# Revit family: Elkay_Drinking-Water_Bottle-Filling-Stations_EZ_Onwall_St1_Asiapac
name_source: partatom
category: Plumbing Fixtures
units: mm (PartAtom-declared; Revit-internal decimal feet)

## family parameters
Always vertical = Yes
Cut with Voids When Loaded = No
Part Type = Normal
Room Calculation Point = No
Round Connector Dimension = Use Diameter
Shared = Yes
Work Plane-Based = No

## types (24) — shared parameters
Installation Location = Indoor
Manufacturer = Elkay
Mounting Type = Wall Mount (On Wall)
Number of Stations = 1
Top Logo Plate = Yes
Version = 1.0.0.0

## per-type parameters (varying)
| type | Activation by | Approx. Shipping Weight | Base With Out Grill | Basin3 | Bottle Filling Station Logo With Out Elkay | Bubbler Style | Chilling Capacity | Dimensions (L x W x H) | EZWSSMJO_Base | EZWSSMJO_plate1 | EZWSSMJO_plate2 | Finish | Finish_1 | Flexiguard Bubbler | Full Load Amps | GreenSpec & Sensor Logo | GreenSpec Logo | Power | Push Button | Rated Watts | Special Features | Top Elkay EZH2@Blue | Vandal Resistant | Without Elkay Top Basin |
| EZWSSMJO | Electronic Bottle Filler Sensor | 32 lbs | No | No | No | No Bubbler | Non-refrigerated | 17 15/16 inch x 8 3/16 inch x 25 7/16 inch | Yes | No | Yes | Stainless Steel | 304 Stainless Steel | No | 1 | No | Yes | 220V/50-60Hz | No | 15 | Antimicrobial, Green Ticker™, Hands Free, Laminar Flow, Real Drain | No | No | No |
| LZS8WSS2K | Electronic Bottle Filler Sensor With Electronic Front And Side Bubbler Pushbar | 71 lbs | Yes | Yes | Yes | Flexi-Guard ® Safety Bubbler | 8.0 GPH | 18 3/8 inch x 19 inch x 39 1/16 inch | No | No | No | Stainless Steel | 304 Stainless Steel | Yes | 3 | Yes | No | 220V/50Hz | Yes | 370 | Hands Free, Visual Filter Monitor, Filtered, Green Ticker™, Laminar Flow, Antimicrobial, Real Drain | Yes | No | Yes |
| LZS8WSVRL2K | Electronic Bottle Filler Sensor With Electronic Front And Side Bubbler Pushbar | 72 lbs | Yes | Yes | Yes | Vandal Resistant | 8.0 GPH | 18 3/8 inch x 19 inch x 39 1/16 inch | No | No | No | Light Gray Granite | Light Gray Granite | No | 3 | Yes | No | 220V/50Hz | Yes | 370 | Hands Free, Visual Filter Monitor, Filtered, Green Ticker™, Laminar Flow, Antimicrobial, Real Drain | Yes | Yes | Yes |
| LZS8WSVRS2K | Electronic Bottle Filler Sensor With Electronic Front And Side Bubbler Pushbar | 72 lbs | Yes | Yes | Yes | Vandal Resistant | 8.0 GPH | 18 3/8 inch x 19 inch x 39 1/16 inch | No | No | No | Stainless Steel | 304 Stainless Steel | No | 3 | Yes | No | 220V/50Hz | Yes | 370 | Hands Free, Visual Filter Monitor, Filtered, Green Ticker™, Laminar Flow, Antimicrobial, Real Drain | Yes | Yes | Yes |
| LZS8WSVRS3K | Electronic Bottle Filler Sensor With Electronic Front And Side Bubbler Pushbar | 72 lbs | Yes | Yes | Yes | Vandal Resistant | 8.0 GPH | 18 3/8 inch x 19 inch x 39 1/16 inch | No | No | No | Stainless Steel | 304 Stainless Steel | No | 3 | Yes | No | 220V/60Hz | Yes | 370 | Hands Free, Visual Filter Monitor, Filtered, Green Ticker™, Laminar Flow, Antimicrobial, Real Drain | Yes | Yes | Yes |
| LZSDWSL2K | Electronic Bottle Filler Sensor With Electronic Front And Side Bubbler Pushbar | 45 lbs | Yes | Yes | Yes | Flexi-Guard ® Safety Bubbler | Non-refrigerated | 18 3/8 inch x 19 inch x 39 1/16 inch | No | No | No | Light Gray Granite | Light Gray Granite | Yes | 2 | Yes | No | 220V/50Hz | Yes | 15 | Hands Free, Visual Filter Monitor, Filtered, Green Ticker™, Laminar Flow, Antimicrobial, Real Drain | Yes | No | Yes |
| LZSDWSL3K | Electronic Bottle Filler Sensor With Electronic Front And Side Bubbler Pushbar | 45 lbs | Yes | Yes | Yes | Flexi-Guard ® Safety Bubbler | Non-refrigerated | 18 3/8 inch x 19 inch x 39 1/16 inch | No | No | No | Light Gray Granite | Light Gray Granite | Yes | 2 | Yes | No | 220V/60Hz | Yes | 15 | Hands Free, Visual Filter Monitor, Filtered, Green Ticker™, Laminar Flow, Antimicrobial, Real Drain | Yes | No | Yes |
| LZSDWSS2K | Electronic Bottle Filler Sensor With Electronic Front And Side Bubbler Pushbar | 45 lbs | Yes | Yes | Yes | Flexi-Guard ® Safety Bubbler | Non-refrigerated | 18 3/8 inch x 19 inch x 39 1/16 inch | No | No | No | Stainless Steel | 304 Stainless Steel | No | 2 | Yes | No | 220V/50Hz | Yes | 15 | Hands Free, Visual Filter Monitor, Filtered, Green Ticker™, Laminar Flow, Antimicrobial, Real Drain | Yes | Yes | Yes |
| LZSDWSS3K | Electronic Bottle Filler Sensor With Electronic Front And Side Bubbler Pushbar | 45 lbs | Yes | Yes | Yes | Flexi-Guard ® Safety Bubbler | Non-refrigerated | 18 3/8 inch x 19 inch x 39 1/16 inch | No | No | No | Stainless Steel | 304 Stainless Steel | No | 2 | Yes | No | 220V/60Hz | Yes | 15 | Hands Free, Visual Filter Monitor, Filtered, Green Ticker™, Laminar Flow, Antimicrobial, Real Drain | Yes | Yes | Yes |
| LZWSSMJO | Electronic Bottle Filler Sensor | 35 lbs | No | No | No | No Bubbler | Non-refrigerated | 17 15/16 inch x 83/16 inch x 25 7/16 inch | Yes | Yes | No | Stainless Steel | 304 Stainless Steel | No | 1 | No | Yes | 220V/50-60Hz | No | 15 | Hands Free, Visual Filter Monitor, Filtered, Green Ticker™, Laminar Flow, Antimicrobial, Real Drain | No | No | No |
| EZS8WSL2K | Electronic Bottle Filler Sensor with Electronic Front and Side Bubbler Pushbar | 68 lbs | Yes | Yes | Yes | Flexi-Guard ® Safety Bubbler | 8.0 GPH | 18 3/8 inch x 19 inch x 39 1/16 inch | No | No | No | Light Gray Granite | Light Gray Granite | Yes | 3 | No | Yes | 220V/50Hz | Yes | 370 | Antimicrobial, Green Ticker™, Hands Free, Laminar Flow, Real Drain | Yes | No | Yes |
| EZS8WSL3K | Electronic Bottle Filler Sensor with Electronic Front and Side Bubbler Pushbar | 68 lbs | Yes | Yes | Yes | Flexi-Guard ® Safety Bubbler | 8.0 GPH | 18 3/8 inch x 19 inch x 39 1/16 inch | No | No | No | Light Gray Granite | Light Gray Granite | Yes | 3 | No | Yes | 220V/60Hz | Yes | 370 | Antimicrobial, Green Ticker™, Hands Free, Laminar Flow, Real Drain | Yes | No | Yes |
| EZS8WSS2K | Electronic Bottle Filler Sensor with Electronic Front and Side Bubbler Pushbar | 68 lbs | Yes | Yes | Yes | Flexi-Guard ® Safety Bubbler | 8.0 GPH | 18 3/8 inch x 19 inch x 39 1/16 inch | No | No | No | Stainless Steel | 304 Stainless Steel | Yes | 3 | No | Yes | 220V/50Hz | Yes | 370 | Antimicrobial, Green Ticker™, Hands Free, Laminar Flow, Real Drain | Yes | No | Yes |
| EZS8WSS3K | Electronic Bottle Filler Sensor with Electronic Front and Side Bubbler Pushbar | 68 lbs | Yes | Yes | Yes | Flexi-Guard ® Safety Bubbler | 8.0 GPH | 18 3/8 inch x 19 inch x 39 1/16 inch | No | No | No | Stainless Steel | 304 Stainless Steel | Yes | 3 | No | Yes | 220V/60Hz | Yes | 370 | Antimicrobial, Green Ticker™, Hands Free, Laminar Flow, Real Drain | Yes | No | Yes |
| EZS8WSVRL2K | Electronic Bottle Filler Sensor with Electronic Front and Side Bubbler Pushbar | 69 lbs | Yes | Yes | Yes | Vandal Resistant | 8.0 GPH | 18 3/8 inch x 19 inch x 39 1/16 inch | No | No | No | Light Gray Granite | Light Gray Granite | No | 3 | No | Yes | 220V/50Hz | Yes | 370 | Antimicrobial, Green Ticker™, Hands Free, Laminar Flow, Real Drain | Yes | Yes | Yes |
| EZS8WSVRL3K | Electronic Bottle Filler Sensor with Electronic Front and Side Bubbler Pushbar | 69 lbs | Yes | Yes | Yes | Vandal Resistant | 8.0 GPH | 18 3/8 inch x 19 inch x 39 1/16 inch | No | No | No | Light Gray Granite | Light Gray Granite | No | 3 | No | Yes | 220V/60Hz | Yes | 370 | Antimicrobial, Green Ticker™, Hands Free, Laminar Flow, Real Drain | Yes | Yes | Yes |
| EZS8WSVRS2K | Electronic Bottle Filler Sensor with Electronic Front and Side Bubbler Pushbar | 69 lbs | Yes | Yes | Yes | Vandal Resistant | 8.0 GPH | 18 3/8 inch x 19 inch x 39 1/16 inch | No | No | No | Stainless Steel | 304 Stainless Steel | No | 3 | No | Yes | 220V/50Hz | Yes | 370 | Antimicrobial, Green Ticker™, Hands Free, Laminar Flow, Real Drain | Yes | Yes | Yes |
| EZS8WSVRS3K | Electronic Bottle Filler Sensor with Electronic Front and Side Bubbler Pushbar | 69 lbs | Yes | Yes | Yes | Vandal Resistant | 8.0 GPH | 18 3/8 inch x 19 inch x 39 1/16 inch | No | No | No | Stainless Steel | 304 Stainless Steel | No | 3 | No | Yes | 220V/60Hz | Yes | 370 | Antimicrobial, Green Ticker™, Hands Free, Laminar Flow, Real Drain | Yes | Yes | Yes |
| LZS8WSL2K | Electronic Bottle Filler Sensor with Electronic Front and Side Bubbler Pushbar | 71 lbs | Yes | Yes | Yes | Flexi-Guard ® Safety Bubbler | 8.0 GPH | 18 3/8 inch x 19 inch x 39 1/16 inch | No | No | No | Light Gray Granite | Light Gray Granite | Yes | 3 | Yes | No | 220V/50Hz | Yes | 370 | Antimicrobial, Filtered, Green Ticker™, Hands Free, Laminar Flow, Real Drain, Visual Filter Monitor | Yes | No | Yes |
| LZS8WSL3K | Electronic Bottle Filler Sensor with Electronic Front and Side Bubbler Pushbar | 71 lbs | Yes | Yes | Yes | Flexi-Guard ® Safety Bubbler | 8.0 GPH | 18 3/8 inch x 19 inch x 39 1/16 inch | No | No | No | Light Gray Granite | Light Gray Granite | Yes | 3 | Yes | No | 220V/60Hz | Yes | 370 | Antimicrobial, Filtered, Green Ticker™, Hands Free, Laminar Flow, Real Drain, Visual Filter Monitor | Yes | No | Yes |
| LZS8WSS2QK | Electronic Bottle Filler Sensor with Electronic Front and Side Bubbler Pushbar | 71 lbs | Yes | Yes | Yes | Flexi-Guard ® Safety Bubbler | 8.0 GPH | 17 7/8 inch x 19 inch x 39 1/16 inch | No | No | No | Stainless Steel | 304 Stainless Steel | Yes | 3 | Yes | No | 240V/50Hz | Yes | 370 | Antimicrobial, Filtered, Green Ticker™, Hands Free, Laminar Flow, Real Drain, Visual Filter Monitor | Yes | No | Yes |
| LZS8WSS3KSA | Electronic Bottle Filler Sensor with Electronic Front and Side Bubbler Pushbar | 71 lbs | Yes | Yes | Yes | Flexi-Guard ® Safety Bubbler | 8.0 GPH | 18 3/8 inch x 19 inch x 39 1/16 inch | No | No | No | Stainless Steel | 304 Stainless Steel | Yes | 3 | Yes | No | 220V/60Hz | Yes | 370 | Antimicrobial, Filtered, Green Ticker™, Hands Free, Laminar Flow, Real Drain, Visual Filter Monitor | Yes | No | Yes |
| LZS8WSVRL3K | Electronic Bottle Filler Sensor with Electronic Front and Side Bubbler Pushbar | 72 lbs | Yes | Yes | Yes | Vandal Resistant | 8.0 GPH | 18 3/8 inch x 19 inch x 39 1/16 inch | No | No | No | Light Gray Granite | Light Gray Granite | No | 3 | Yes | No | 220V/60Hz | Yes | 370 | Antimicrobial, Filtered, Green Ticker™, Hands Free, Laminar Flow, Real Drain, Visual Filter Monitor | Yes | Yes | Yes |
| LZS8WSS3K | Electronic Bottle Filler Sensor with Electronic Front and Side Bubbler Pushbar | 71 lbs | Yes | Yes | Yes | Flexi-Guard ® Safety Bubbler | 8.0 GPH | 18 3/8 inch x 19 inch x 39 1/16 inch | No | No | No | Stainless Steel | 304 Stainless Steel | Yes | 3 | Yes | No | 220V/60Hz | Yes | 370 | Antimicrobial, Filtered, Green Ticker™, Hands Free, Laminar Flow, Real Drain, Visual Filter Monitor | Yes | No | Yes |

note: column(s) folded — value = type name in every type: Model

## geometry (parser evidence)
native form markers: Sweep x96
no freeform markers — native parametric forms only
